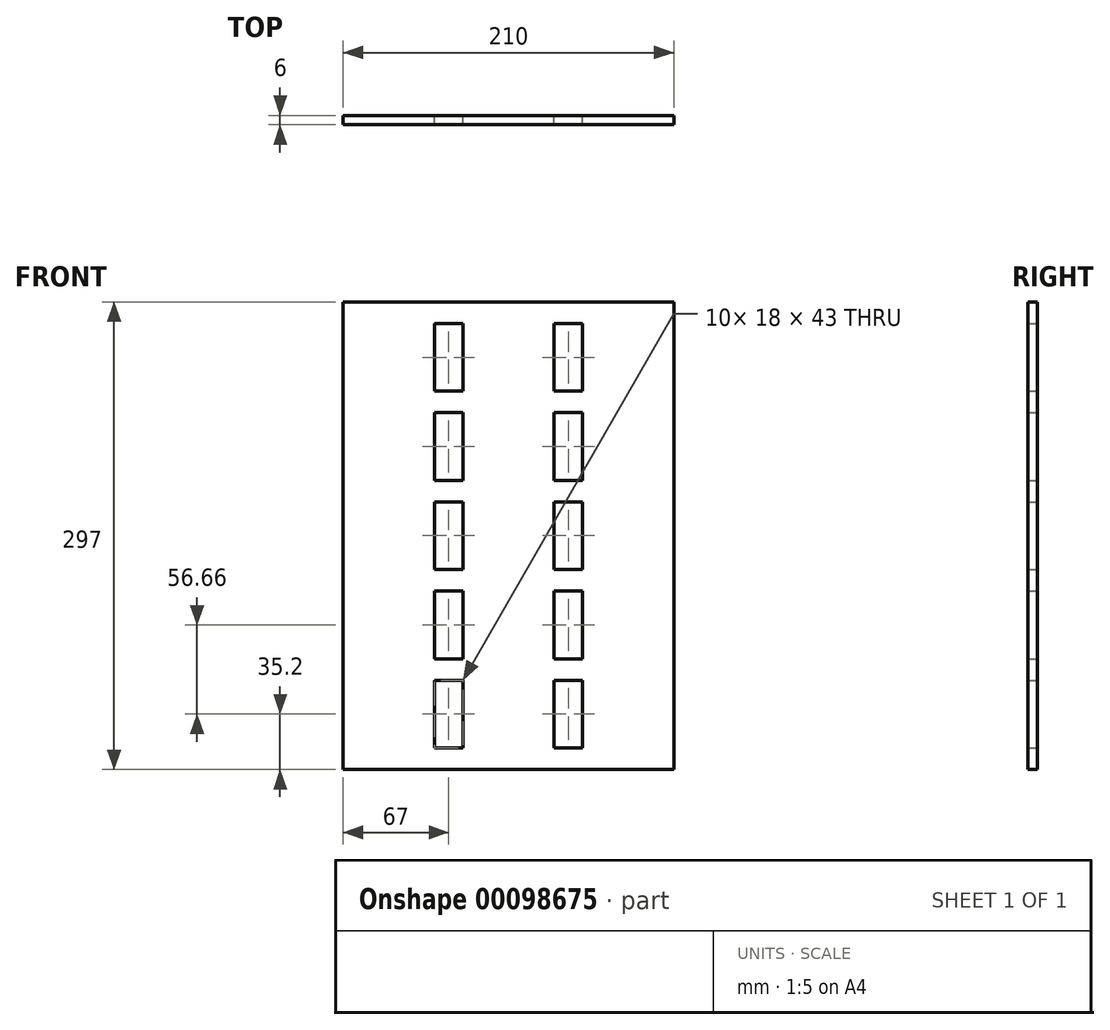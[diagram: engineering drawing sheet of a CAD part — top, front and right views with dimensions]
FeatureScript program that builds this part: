
annotation { "Feature Type Name" : "Feature", "Feature Type Description" : "" }
export const myFeature = defineFeature(function(context is Context, id is Id, definition is map)
    precondition{}
    {
        {
            var Q0;
            Q0=qCreatedBy(makeId("Front.planeOp"),FACE);
            var sketch = newSketch(context, id + "F0", { "sketchPlane" : qUnion([Q0])});
            skLineSegment(sketch, "E0.bottom", {"start": v(88.33, -148.5) * mm, "end": v(-121.67, -148.5) * mm});
            skLineSegment(sketch, "E0.top", {"start": v(88.33, 148.5) * mm, "end": v(-121.67, 148.5) * mm});
            skLineSegment(sketch, "E0.left", {"start": v(88.33, -148.5) * mm, "end": v(88.33, 148.5) * mm});
            skLineSegment(sketch, "E0.right", {"start": v(-121.67, -148.5) * mm, "end": v(-121.67, 148.5) * mm});
            skLineSegment(sketch, "E1.bottom", {"start": v(-45.67, 91.84) * mm, "end": v(-63.67, 91.84) * mm});
            skLineSegment(sketch, "E1.top", {"start": v(-45.67, 134.84) * mm, "end": v(-63.67, 134.84) * mm});
            skLineSegment(sketch, "E1.left", {"start": v(-45.67, 91.84) * mm, "end": v(-45.67, 134.84) * mm});
            skLineSegment(sketch, "E1.right", {"start": v(-63.67, 91.84) * mm, "end": v(-63.67, 134.84) * mm});
            skPoint(sketch, "E1.middle", {"position": v(-54.67, 113.34) * mm});
            skLineSegment(sketch, "E2.0.1.0", {"start": v(-45.67, 35.18) * mm, "end": v(-45.67, 78.18) * mm});
            skLineSegment(sketch, "E2.0.1.1", {"start": v(-45.67, 78.18) * mm, "end": v(-63.67, 78.18) * mm});
            skLineSegment(sketch, "E2.0.1.2", {"start": v(-63.67, 35.18) * mm, "end": v(-63.67, 78.18) * mm});
            skLineSegment(sketch, "E2.0.1.3", {"start": v(-45.67, 35.18) * mm, "end": v(-63.67, 35.18) * mm});
            skLineSegment(sketch, "E2.0.2.0", {"start": v(-45.67, -21.48) * mm, "end": v(-45.67, 21.52) * mm});
            skLineSegment(sketch, "E2.0.2.1", {"start": v(-45.67, 21.52) * mm, "end": v(-63.67, 21.52) * mm});
            skLineSegment(sketch, "E2.0.2.2", {"start": v(-63.67, -21.48) * mm, "end": v(-63.67, 21.52) * mm});
            skLineSegment(sketch, "E2.0.2.3", {"start": v(-45.67, -21.48) * mm, "end": v(-63.67, -21.48) * mm});
            skLineSegment(sketch, "E2.0.3.0", {"start": v(-45.67, -78.14) * mm, "end": v(-45.67, -35.14) * mm});
            skLineSegment(sketch, "E2.0.3.1", {"start": v(-45.67, -35.14) * mm, "end": v(-63.67, -35.14) * mm});
            skLineSegment(sketch, "E2.0.3.2", {"start": v(-63.67, -78.14) * mm, "end": v(-63.67, -35.14) * mm});
            skLineSegment(sketch, "E2.0.3.3", {"start": v(-45.67, -78.14) * mm, "end": v(-63.67, -78.14) * mm});
            skLineSegment(sketch, "E2.0.4.0", {"start": v(-45.67, -134.8) * mm, "end": v(-45.67, -91.8) * mm});
            skLineSegment(sketch, "E2.0.4.1", {"start": v(-45.67, -91.8) * mm, "end": v(-63.67, -91.8) * mm});
            skLineSegment(sketch, "E2.0.4.2", {"start": v(-63.67, -134.8) * mm, "end": v(-63.67, -91.8) * mm});
            skLineSegment(sketch, "E2.0.4.3", {"start": v(-45.67, -134.8) * mm, "end": v(-63.67, -134.8) * mm});
            skLineSegment(sketch, "E2.1.0.0", {"start": v(30.33, 91.84) * mm, "end": v(30.33, 134.84) * mm});
            skLineSegment(sketch, "E2.1.0.1", {"start": v(30.33, 134.84) * mm, "end": v(12.33, 134.84) * mm});
            skLineSegment(sketch, "E2.1.0.2", {"start": v(12.33, 91.84) * mm, "end": v(12.33, 134.84) * mm});
            skLineSegment(sketch, "E2.1.0.3", {"start": v(30.33, 91.84) * mm, "end": v(12.33, 91.84) * mm});
            skLineSegment(sketch, "E2.1.1.0", {"start": v(30.33, 35.18) * mm, "end": v(30.33, 78.18) * mm});
            skLineSegment(sketch, "E2.1.1.1", {"start": v(30.33, 78.18) * mm, "end": v(12.33, 78.18) * mm});
            skLineSegment(sketch, "E2.1.1.2", {"start": v(12.33, 35.18) * mm, "end": v(12.33, 78.18) * mm});
            skLineSegment(sketch, "E2.1.1.3", {"start": v(30.33, 35.18) * mm, "end": v(12.33, 35.18) * mm});
            skLineSegment(sketch, "E2.1.2.0", {"start": v(30.33, -21.48) * mm, "end": v(30.33, 21.52) * mm});
            skLineSegment(sketch, "E2.1.2.1", {"start": v(30.33, 21.52) * mm, "end": v(12.33, 21.52) * mm});
            skLineSegment(sketch, "E2.1.2.2", {"start": v(12.33, -21.48) * mm, "end": v(12.33, 21.52) * mm});
            skLineSegment(sketch, "E2.1.2.3", {"start": v(30.33, -21.48) * mm, "end": v(12.33, -21.48) * mm});
            skLineSegment(sketch, "E2.1.3.0", {"start": v(30.33, -78.14) * mm, "end": v(30.33, -35.14) * mm});
            skLineSegment(sketch, "E2.1.3.1", {"start": v(30.33, -35.14) * mm, "end": v(12.33, -35.14) * mm});
            skLineSegment(sketch, "E2.1.3.2", {"start": v(12.33, -78.14) * mm, "end": v(12.33, -35.14) * mm});
            skLineSegment(sketch, "E2.1.3.3", {"start": v(30.33, -78.14) * mm, "end": v(12.33, -78.14) * mm});
            skLineSegment(sketch, "E2.1.4.0", {"start": v(30.33, -134.8) * mm, "end": v(30.33, -91.8) * mm});
            skLineSegment(sketch, "E2.1.4.1", {"start": v(30.33, -91.8) * mm, "end": v(12.33, -91.8) * mm});
            skLineSegment(sketch, "E2.1.4.2", {"start": v(12.33, -134.8) * mm, "end": v(12.33, -91.8) * mm});
            skLineSegment(sketch, "E2.1.4.3", {"start": v(30.33, -134.8) * mm, "end": v(12.33, -134.8) * mm});
            skLineSegment(sketch, "E2.direction1", {"start": v(-45.67, 91.84) * mm, "end": v(30.33, 91.84) * mm, "construction": true});
            skLineSegment(sketch, "E2.direction2", {"start": v(-45.67, 91.84) * mm, "end": v(-45.67, 35.18) * mm, "construction": true});
            skSolve(sketch);
        }
        {
            var Q0;
            Q0 = qSketchRegion(id + "F0", true);
            extrude(context, id + "F1", {"entities" : qUnion([Q0]), "endBound" : BoundingType.SYMMETRIC, "depth" : 6 * mm});
        }
    });
